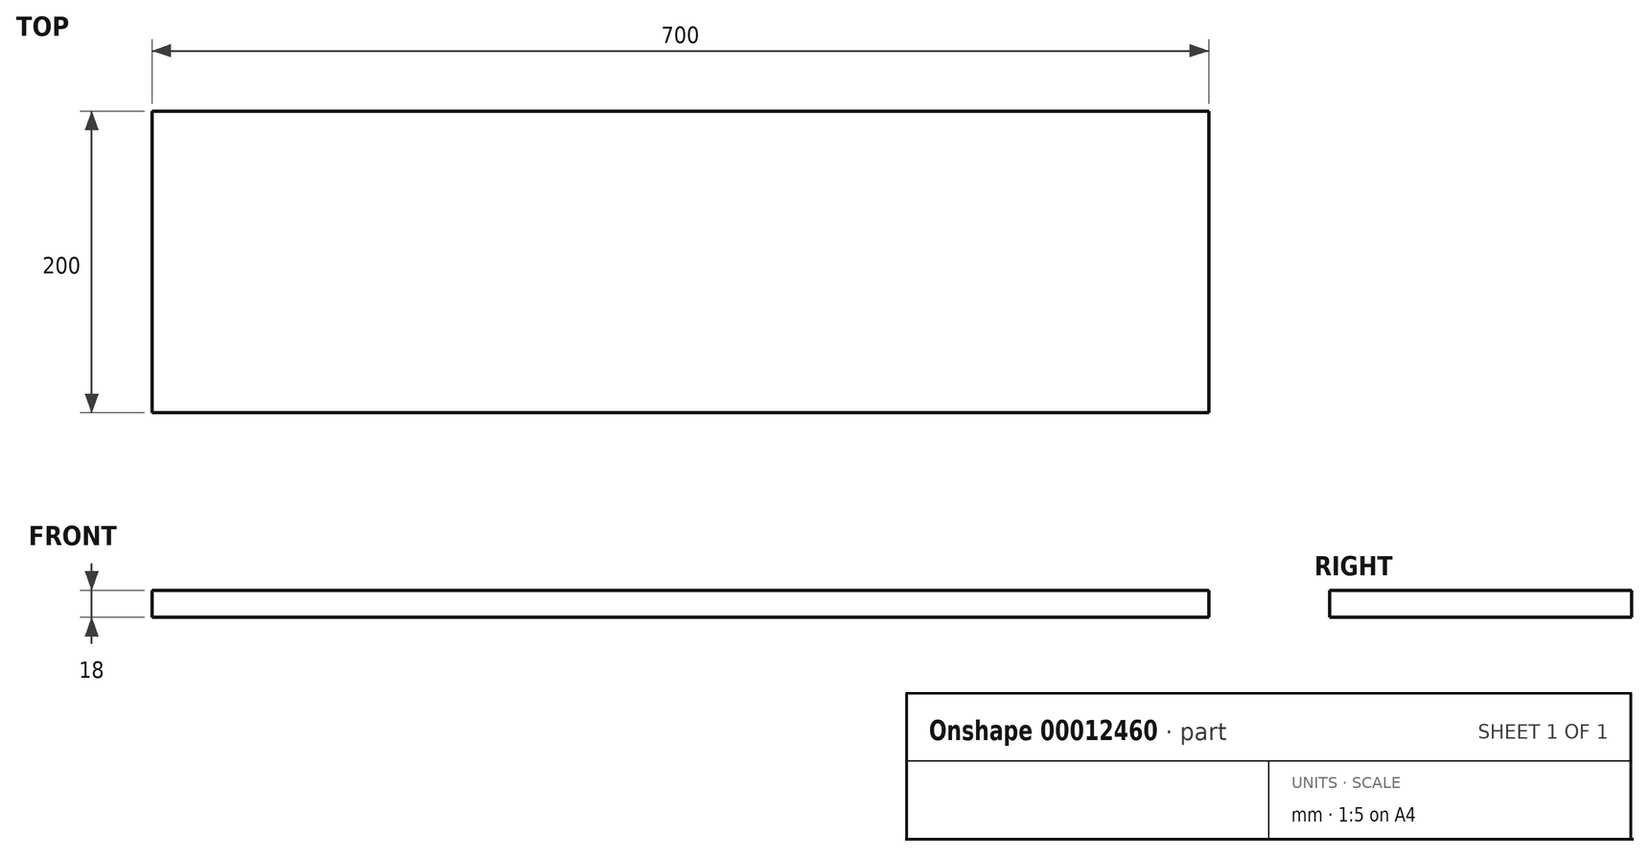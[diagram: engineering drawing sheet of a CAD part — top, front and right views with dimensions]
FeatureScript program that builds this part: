
annotation { "Feature Type Name" : "Feature", "Feature Type Description" : "" }
export const myFeature = defineFeature(function(context is Context, id is Id, definition is map)
    precondition{}
    {
        {
            var Q0;
            Q0=qCreatedBy(makeId("Top.planeOp"),FACE);
            var sketch = newSketch(context, id + "F0", { "sketchPlane" : qUnion([Q0])});
            skLineSegment(sketch, "E0.bottom", {"start": v(0, 0) * mm, "end": v(700, 0) * mm});
            skLineSegment(sketch, "E0.top", {"start": v(0, 200) * mm, "end": v(700, 200) * mm});
            skLineSegment(sketch, "E0.left", {"start": v(0, 0) * mm, "end": v(0, 200) * mm});
            skLineSegment(sketch, "E0.right", {"start": v(700, 0) * mm, "end": v(700, 200) * mm});
            skSolve(sketch);
        }
        {
            var Q0;
            Q0=makeQuery(id+"F0.imprint","IMPRINT",FACE,{"disambiguationData":[TD([[makeQuery(id+"F0.imprint","IMPRINT",EDGE,{"derivedFrom":sQuery(id+"F0.wireOp",EDGE,"E0.bottom")}),1.0]])]});
            extrude(context, id + "F1", {"entities" : qUnion([Q0]), "depth" : 18 * mm});
        }
    });
